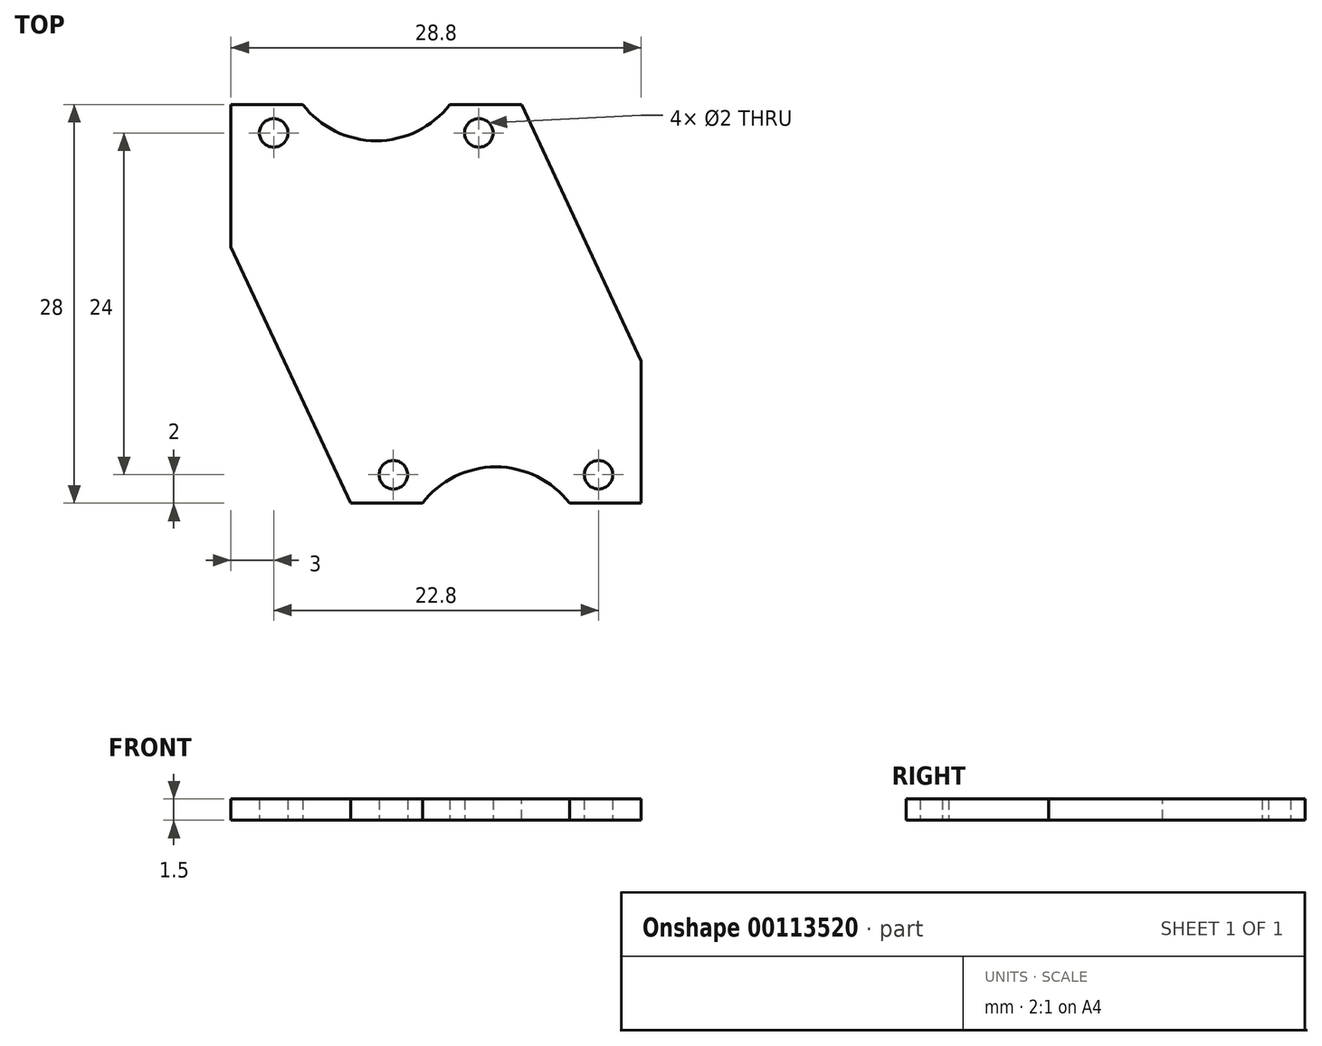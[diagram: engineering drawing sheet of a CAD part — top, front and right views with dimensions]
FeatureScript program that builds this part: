
annotation { "Feature Type Name" : "Feature", "Feature Type Description" : "" }
export const myFeature = defineFeature(function(context is Context, id is Id, definition is map)
    precondition{}
    {
        {
            var Q0;
            Q0=qCreatedBy(makeId("Top.planeOp"),FACE);
            var sketch = newSketch(context, id + "F0", { "sketchPlane" : qUnion([Q0])});
            skLineSegment(sketch, "E0.bottom", {"start": v(14.4, -14) * mm, "end": v(9.36, -14) * mm});
            skLineSegment(sketch, "E0.top", {"start": v(14.4, 14) * mm, "end": v(0.96, 14) * mm});
            skLineSegment(sketch, "E0.left", {"start": v(14.4, -14) * mm, "end": v(14.4, 14) * mm});
            skLineSegment(sketch, "E0.right", {"start": v(-14.4, -14) * mm, "end": v(-14.4, 14) * mm});
            skPoint(sketch, "E0.middle", {"position": v(0, 0) * mm});
            skCircle(sketch, "E1", {"center": v(-11.4, 12) * mm, "radius": 1 * mm});
            skCircle(sketch, "E2", {"center": v(3, 12) * mm, "radius": 1 * mm});
            skCircle(sketch, "E3", {"center": v(-4.2, 36.9) * mm, "radius": 6 * mm, "construction": true});
            skLineSegment(sketch, "E4", {"start": v(-11.4, 12) * mm, "end": v(3, 12) * mm, "construction": true});
            skPoint(sketch, "E5", {"position": v(-4.2, 12) * mm});
            skCircle(sketch, "E6.MirrorC", {"center": v(11.4, 12) * mm, "radius": 1 * mm, "construction": true});
            skCircle(sketch, "E7.MirrorC", {"center": v(-3, 12) * mm, "radius": 1 * mm, "construction": true});
            skCircle(sketch, "E8.MirrorC", {"center": v(-3, -12) * mm, "radius": 1 * mm});
            skCircle(sketch, "E9.MirrorC", {"center": v(11.4, -12) * mm, "radius": 1 * mm});
            skLineSegment(sketch, "E10", {"start": v(-3, -12) * mm, "end": v(11.4, -12) * mm, "construction": true});
            skPoint(sketch, "E11", {"position": v(4.2, -12) * mm});
            skCircle(sketch, "E12", {"center": v(4.2, -36.9) * mm, "radius": 6 * mm, "construction": true});
            skArc(sketch, "E13", {"start": v(-9.36, 14) * mm, "mid": v(-4.2, 11.45) * mm, "end": v(0.96, 14) * mm});
            skLineSegment(sketch, "E14.trimOffspring", {"start": v(-9.36, 14) * mm, "end": v(-14.4, 14) * mm});
            skArc(sketch, "E15.MirrorCS", {"start": v(-9.36, -14) * mm, "mid": v(-4.2, -11.45) * mm, "end": v(0.96, -14) * mm, "construction": true});
            skArc(sketch, "E16.MirrorCS", {"start": v(9.36, -14) * mm, "mid": v(4.2, -11.45) * mm, "end": v(-0.96, -14) * mm});
            skLineSegment(sketch, "E17.trimOffspring", {"start": v(-0.96, -14) * mm, "end": v(-14.4, -14) * mm});
            skSolve(sketch);
        }
        {
            var Q0;
            Q0=qSketchRegion(id+"F0",true);
            extrude(context, id + "F1", {"entities" : qUnion([Q0]), "depth" : 1.5 * mm});
        }
        {
            var Q0;
            Q0=makeQuery(id+"F1.opExtrude","CAP_FACE",FACE,{"disambiguationData":[OSD([sQuery(id+"F0.wireOp",EDGE,"E0.bottom"),sQuery(id+"F0.wireOp",EDGE,"E0.top"),sQuery(id+"F0.wireOp",EDGE,"E0.left"),sQuery(id+"F0.wireOp",EDGE,"E0.right"),sQuery(id+"F0.wireOp",EDGE,"E1"),sQuery(id+"F0.wireOp",EDGE,"E2"),sQuery(id+"F0.wireOp",EDGE,"E8.MirrorC"),sQuery(id+"F0.wireOp",EDGE,"E9.MirrorC")])],"isStart":false});
            var sketch = newSketch(context, id + "F2", { "sketchPlane" : qUnion([Q0])});
            skPoint(sketch, "E18", {"position": v(-11.4, 12) * mm});
            skPoint(sketch, "E19", {"position": v(-3, -12) * mm});
            skLineSegment(sketch, "E20", {"start": v(-14.4, 4) * mm, "end": v(-6, -14) * mm});
            skLineSegment(sketch, "E21", {"start": v(-14.4, 4) * mm, "end": v(-14.4, -14) * mm});
            skLineSegment(sketch, "E22", {"start": v(-14.4, -14) * mm, "end": v(-6, -14) * mm});
            skLineSegment(sketch, "E23.MirrorCS", {"start": v(14.4, 4) * mm, "end": v(14.4, -14) * mm, "construction": true});
            skLineSegment(sketch, "E24.MirrorCS", {"start": v(14.4, 4) * mm, "end": v(6, -14) * mm, "construction": true});
            skLineSegment(sketch, "E25.MirrorCS", {"start": v(14.4, -14) * mm, "end": v(6, -14) * mm, "construction": true});
            skLineSegment(sketch, "E26.MirrorCS", {"start": v(14.4, -4) * mm, "end": v(6, 14) * mm});
            skLineSegment(sketch, "E27.MirrorCS", {"start": v(14.4, -4) * mm, "end": v(14.4, 14) * mm});
            skLineSegment(sketch, "E28.MirrorCS", {"start": v(14.4, 14) * mm, "end": v(6, 14) * mm});
            skSolve(sketch);
        }
        {
            var Q0;
            Q0=qSketchRegion(id+"F2",true);
            extrude(context, id + "F3", {"entities" : qUnion([Q0]), "operationType" : NewBodyOperationType.REMOVE, "endBound" : BoundingType.UP_TO_NEXT, "oppositeDirection" : true, "depth" : 25 * mm});
        }
    });
